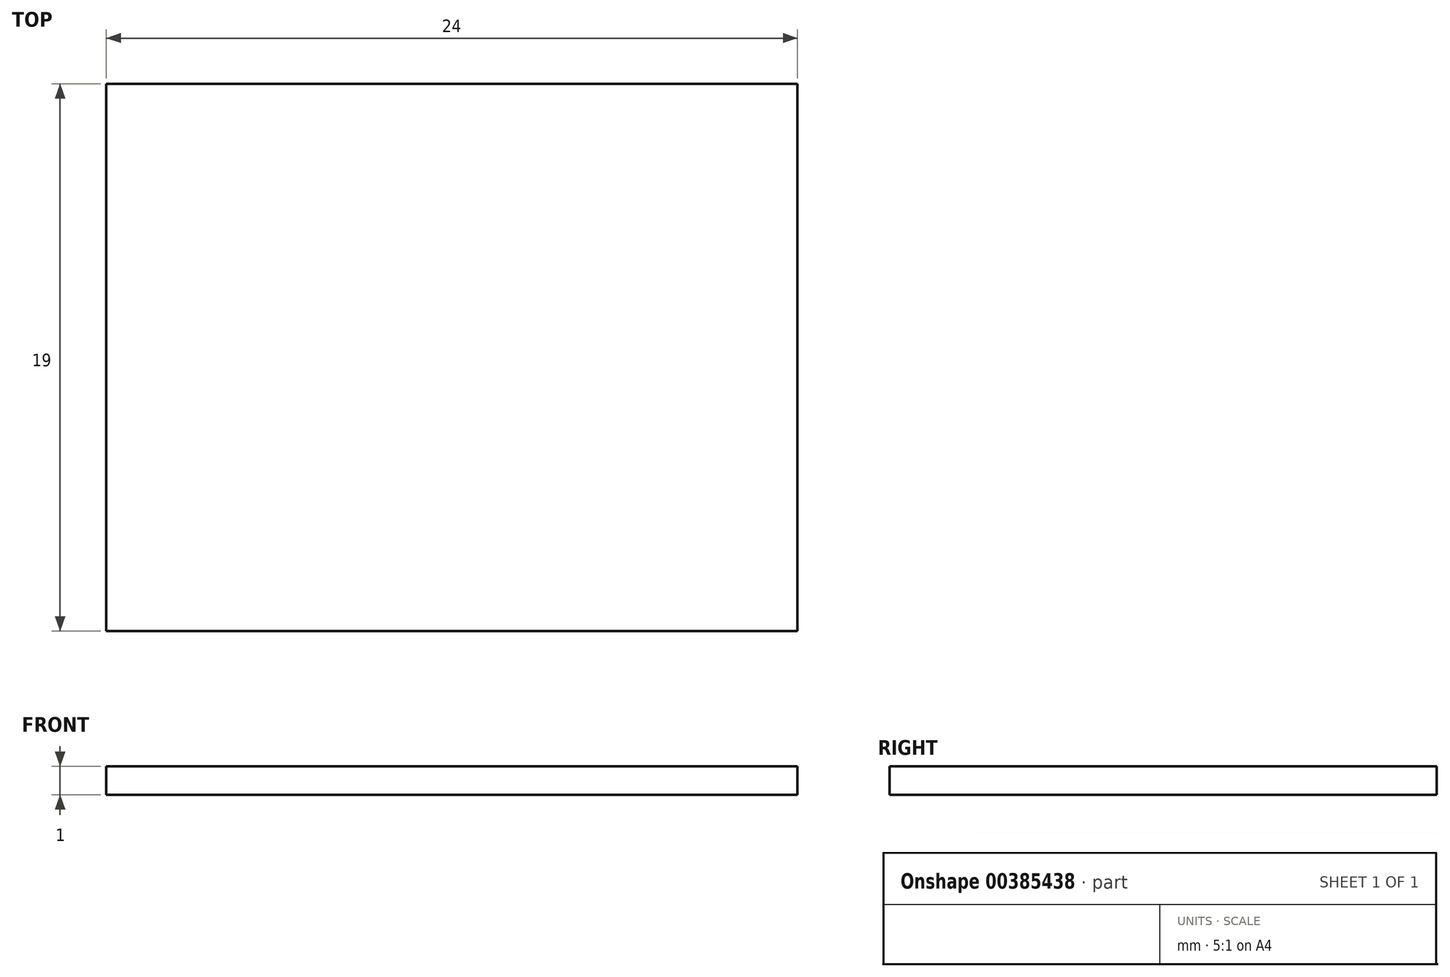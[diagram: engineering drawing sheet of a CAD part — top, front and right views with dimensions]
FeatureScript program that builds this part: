
annotation { "Feature Type Name" : "Feature", "Feature Type Description" : "" }
export const myFeature = defineFeature(function(context is Context, id is Id, definition is map)
    precondition{}
    {
        {
            var Q0;
            Q0=qCreatedBy(makeId("Top.planeOp"),FACE);
            var sketch = newSketch(context, id + "F0", { "sketchPlane" : qUnion([Q0])});
            skLineSegment(sketch, "E0.bottom", {"start": v(54, -20) * mm, "end": v(-54, -20) * mm});
            skLineSegment(sketch, "E0.top", {"start": v(54, 20) * mm, "end": v(-54, 20) * mm});
            skLineSegment(sketch, "E0.left", {"start": v(54, -20) * mm, "end": v(54, 20) * mm});
            skLineSegment(sketch, "E0.right", {"start": v(-54, -20) * mm, "end": v(-54, 20) * mm});
            skPoint(sketch, "E0.middle", {"position": v(0, 0) * mm});
            skLineSegment(sketch, "E1.bottom", {"start": v(54, -20) * mm, "end": v(30, -20) * mm});
            skLineSegment(sketch, "E1.top", {"start": v(54, -1) * mm, "end": v(30, -1) * mm});
            skLineSegment(sketch, "E1.left", {"start": v(54, -20) * mm, "end": v(54, -1) * mm});
            skLineSegment(sketch, "E1.right", {"start": v(30, -20) * mm, "end": v(30, -1) * mm});
            skSolve(sketch);
        }
        {
            var Q0;
            Q0=makeQuery(id+"F0.imprint","IMPRINT",FACE,{"disambiguationData":[TD([[makeQuery(id+"F0.imprint","IMPRINT",EDGE,{"derivedFrom":sQuery(id+"F0.wireOp",EDGE,"E0.bottom")}),-1.0]])]});
            extrude(context, id + "F1", {"entities" : qUnion([Q0]), "depth" : 1 * mm});
        }
    });
